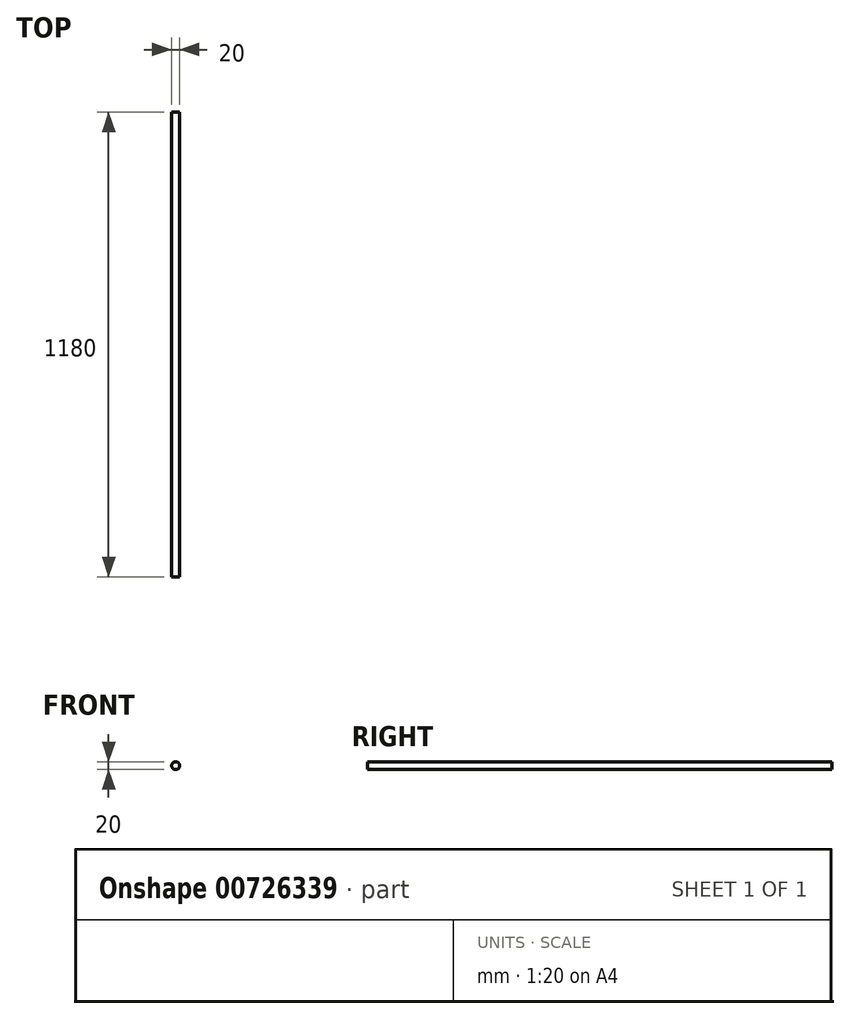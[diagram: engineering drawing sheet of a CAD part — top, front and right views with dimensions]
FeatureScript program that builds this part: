
annotation { "Feature Type Name" : "Feature", "Feature Type Description" : "" }
export const myFeature = defineFeature(function(context is Context, id is Id, definition is map)
    precondition{}
    {
        {
            var Q0;
            Q0=qCreatedBy(makeId("Front.planeOp"),FACE);
            var sketch = newSketch(context, id + "F0", { "sketchPlane" : qUnion([Q0])});
            skCircle(sketch, "E0", {"center": v(-18.7, 10.1) * mm, "radius": 10 * mm});
            skSolve(sketch);
        }
        {
            var Q0;
            Q0 = qSketchRegion(id + "F0", true);
            extrude(context, id + "F1", {"entities" : qUnion([Q0]), "depth" : 1180 * mm, "offsetDistance" : 25 * mm});
        }
    });
